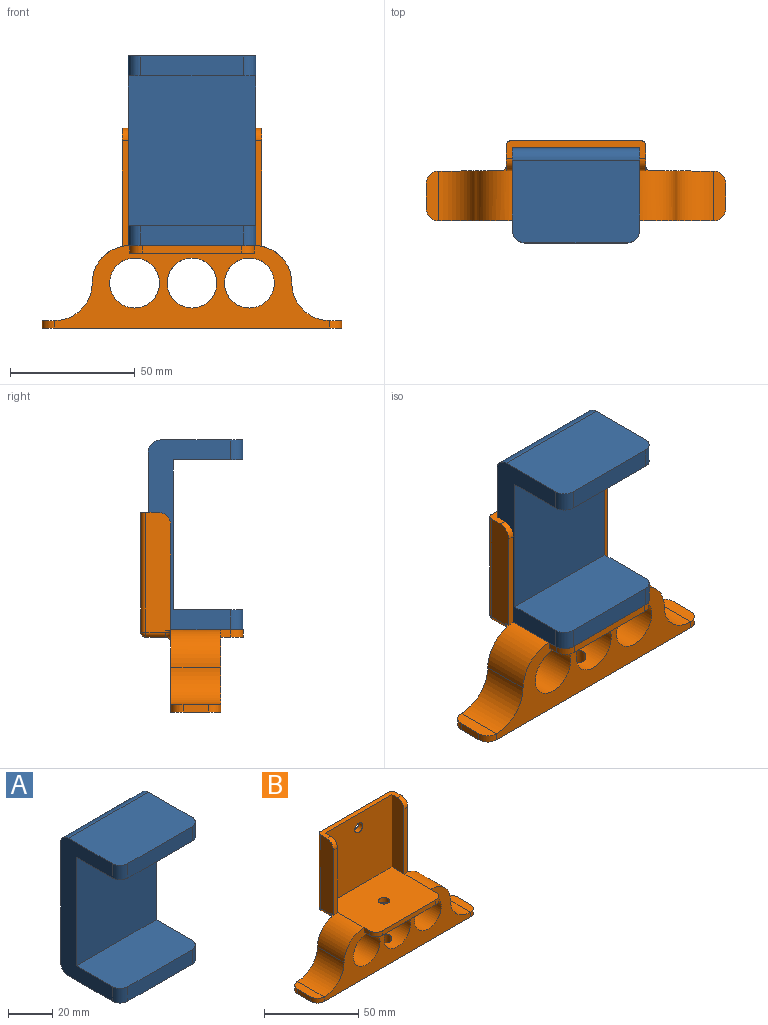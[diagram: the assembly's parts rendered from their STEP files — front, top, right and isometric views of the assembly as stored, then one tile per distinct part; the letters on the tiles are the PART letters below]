
ASSEMBLY  parts=2 mates=1
PART A: 16 faces, bbox 51x38x76 mm
  f0: plane 41x8mm, normal (0,-1,0), area 328mm2, adj f2,f7,f14,f15
  f1: plane 76x33mm, normal (1,0,0), area 1117.3mm2, adj f2,f4,f6,f7,f8,f9,f11,f12
  f2: plane 51x33mm, normal (0,0,1), area 1672.3mm2, adj f0,f1,f3,f13,f14,f15
  f3: plane 76x33mm, normal (-1,0,0), area 1117.3mm2, adj f2,f4,f6,f7,f8,f9,f10,f12
  f4: plane 51x33mm, normal (0,0,-1), area 1672.3mm2, adj f1,f3,f5,f10,f11,f12
  f5: plane 41x8mm, normal (0,-1,0), area 328mm2, adj f4,f8,f10,f11
  f6: plane 66x51mm, normal (0,1,0), area 3366mm2, adj f1,f3,f12,f13
  f7: plane 51x28mm, normal (0,0,-1), area 1417.3mm2, adj f0,f1,f3,f9,f14,f15
  f8: plane 51x28mm, normal (0,0,1), area 1417.3mm2, adj f1,f3,f5,f9,f10,f11
  f9: plane 60x51mm, normal (0,-1,0), area 3060mm2, adj f1,f3,f7,f8
  f10: cylinder r=5mm len=8mm, axis (0,0,1), area 62.8mm2, adj f3,f4,f5,f8
  f11: cylinder r=5mm len=8mm, axis (0,0,-1), area 62.8mm2, adj f1,f4,f5,f8
  f12: cylinder r=5mm len=51mm, axis (1,0,0), area 400.6mm2, adj f1,f3,f4,f6
  f13: cylinder r=5mm len=51mm, axis (-1,0,0), area 400.6mm2, adj f1,f2,f3,f6
  f14: cylinder r=5mm len=8mm, axis (0,0,1), area 62.8mm2, adj f0,f2,f3,f7
  f15: cylinder r=5mm len=8mm, axis (0,0,-1), area 62.8mm2, adj f0,f1,f2,f7
PART B: 54 faces, bbox 120x41x80 mm
  f0: plane 110x32.14mm, normal (0,1,0), area 1497.2mm2, adj f1,f4,f7,f8,f9,f10,f11,f12
  f1: cylinder r=10mm len=20mm, axis (0,1,0), area 1124.1mm2, adj f0,f13,f22,f23
  f2: plane 20x5mm, normal (0,0,1), area 89.3mm2, adj f3,f11,f27,f29
  f3: plane 10x3mm, normal (-1,0,0), area 30mm2, adj f2,f4,f27,f29
  f4: plane 120x20mm, normal (0,0,-1), area 2328.3mm2, adj f0,f3,f5,f13,f23,f26,f27,f28
  f5: plane 10x3mm, normal (1,0,0), area 30mm2, adj f4,f6,f26,f28
  f6: plane 20x5mm, normal (0,0,1), area 89.3mm2, adj f5,f7,f26,f28
  f7: cylinder r=15mm len=20mm, axis (0,1,0), area 471.2mm2, adj f0,f6,f8,f13
  f8: cylinder r=15mm len=22mm, axis (0,1,0), area 472.1mm2, adj f0,f7,f13,f15,f35,f36,f44
  f9: cylinder r=15mm len=22mm, axis (0,1,0), area 472.1mm2, adj f0,f11,f13,f15,f38,f40,f53
  f10: cylinder r=10mm len=20mm, axis (0,1,0), area 1256.6mm2, adj f0,f13
  f11: cylinder r=15mm len=20mm, axis (0,1,0), area 471.2mm2, adj f0,f2,f9,f13
  f12: cylinder r=10mm len=20mm, axis (0,1,0), area 1256.6mm2, adj f0,f13
  f13: plane 110x33mm, normal (0,-1,0), area 1637.5mm2, adj f1,f4,f7,f8,f9,f10,f11,f12
  f14: plane 52x8mm, normal (0,0,-1), area 416mm2, adj f45,f46,f50,f51
  f15: plane 50x38mm, normal (0,0,1), area 1861mm2, adj f8,f9,f16,f18,f19,f20,f24,f25
  f16: plane 4x3mm, normal (-1,0,0), area 12mm2, adj f13,f15,f17,f24
  f17: plane 50x9mm, normal (0,0,-1), area 439.3mm2, adj f13,f16,f18,f19,f24,f25
  f18: plane 4x3mm, normal (1,0,0), area 12mm2, adj f13,f15,f17,f25
  f19: plane 40x3mm, normal (0,-1,0), area 120mm2, adj f15,f17,f24,f25
  f20: cylinder r=3mm len=6mm, axis (0,0,-1), area 56.5mm2, adj f15,f21
  f21: plane 10x10mm, normal (0,0,-1), area 50.3mm2, adj f20,f22
  f22: cylinder r=5mm len=10mm, axis (0,0,-1), area 83.5mm2, adj f1,f21
  f23: cylinder r=4mm len=8.84mm, axis (0,0,-1), area 211.4mm2, adj f1,f4
  f24: cylinder r=5mm len=5mm, axis (0,0,1), area 23.6mm2, adj f15,f16,f17,f19
  f25: cylinder r=5mm len=5mm, axis (0,0,-1), area 23.6mm2, adj f15,f17,f18,f19
  f26: cylinder r=5mm len=5mm, axis (0,0,1), area 23.6mm2, adj f0,f4,f5,f6
  f27: cylinder r=5mm len=5mm, axis (0,0,-1), area 23.6mm2, adj f0,f2,f3,f4
  f28: cylinder r=5mm len=5mm, axis (0,0,-1), area 23.6mm2, adj f4,f5,f6,f13
  f29: cylinder r=5mm len=5mm, axis (0,0,1), area 23.6mm2, adj f2,f3,f4,f13
  f30: plane 50x47mm, normal (0,-1,0), area 2321.7mm2, adj f15,f31,f33,f34,f39
  f31: plane 56x7mm, normal (0,0,1), area 190.3mm2, adj f30,f32,f34,f36,f37,f39,f40,f41
  f32: plane 52x48mm, normal (0,1,0), area 2467.7mm2, adj f31,f33,f42,f46,f47
  f33: cylinder r=3mm len=6mm, axis (0,-1,0), area 56.5mm2, adj f30,f32
  f34: plane 47x9mm, normal (-1,0,0), area 417.6mm2, adj f15,f30,f31,f35,f37
  f35: plane 42.3x3mm, normal (0,-1,0), area 126.3mm2, adj f8,f34,f36,f37
  f36: plane 48x10mm, normal (1,0,0), area 473.2mm2, adj f8,f31,f35,f37,f42,f44,f45
  f37: cylinder r=5mm len=5mm, axis (1,0,0), area 23.6mm2, adj f31,f34,f35,f36
  f38: plane 42.3x3mm, normal (0,-1,0), area 126.3mm2, adj f9,f39,f40,f41
  f39: plane 47x9mm, normal (1,0,0), area 417.6mm2, adj f15,f30,f31,f38,f41
  f40: plane 48x10mm, normal (-1,0,0), area 473.2mm2, adj f9,f31,f38,f41,f47,f51,f53
  f41: cylinder r=5mm len=5mm, axis (-1,0,0), area 23.6mm2, adj f31,f38,f39,f40
  f42: cylinder r=2mm len=48mm, axis (0,0,-1), area 150.8mm2, adj f31,f32,f36,f43
  f43: sphere r=2mm, area 6.3mm2, adj f42,f45,f46
  f44: cylinder r=2mm len=2mm, axis (0,0,-1), area 1.6mm2, adj f0,f8,f36,f48
  f45: cylinder r=2mm len=8mm, axis (0,-1,0), area 25.1mm2, adj f14,f36,f43,f48
  f46: cylinder r=2mm len=52mm, axis (1,0,0), area 163.4mm2, adj f14,f32,f43,f49
  f47: cylinder r=2mm len=48mm, axis (0,0,1), area 150.8mm2, adj f31,f32,f40,f49
  f48: torus R=4mm, axis (0,-1,0), area 13.5mm2, adj f0,f44,f45,f50
  f49: sphere r=2mm, area 6.3mm2, adj f46,f47,f51
  f50: cylinder r=2mm len=52mm, axis (-1,0,0), area 163.4mm2, adj f0,f14,f48,f52
  f51: cylinder r=2mm len=8mm, axis (0,-1,0), area 25.1mm2, adj f14,f40,f49,f52
  f52: torus R=4mm, axis (0,-1,0), area 13.5mm2, adj f0,f50,f51,f53
  f53: cylinder r=2mm len=2mm, axis (0,0,1), area 1.6mm2, adj f0,f9,f40,f52
PLACE A t=(-30.44,-32.93,72.12)mm
PLACE B t=(-30.44,-33.03,4.12)mm
MATE parallel B.f15 <-> A.f4  axis (0,0,1) through (-30.44,-32.93,34.12)mm
